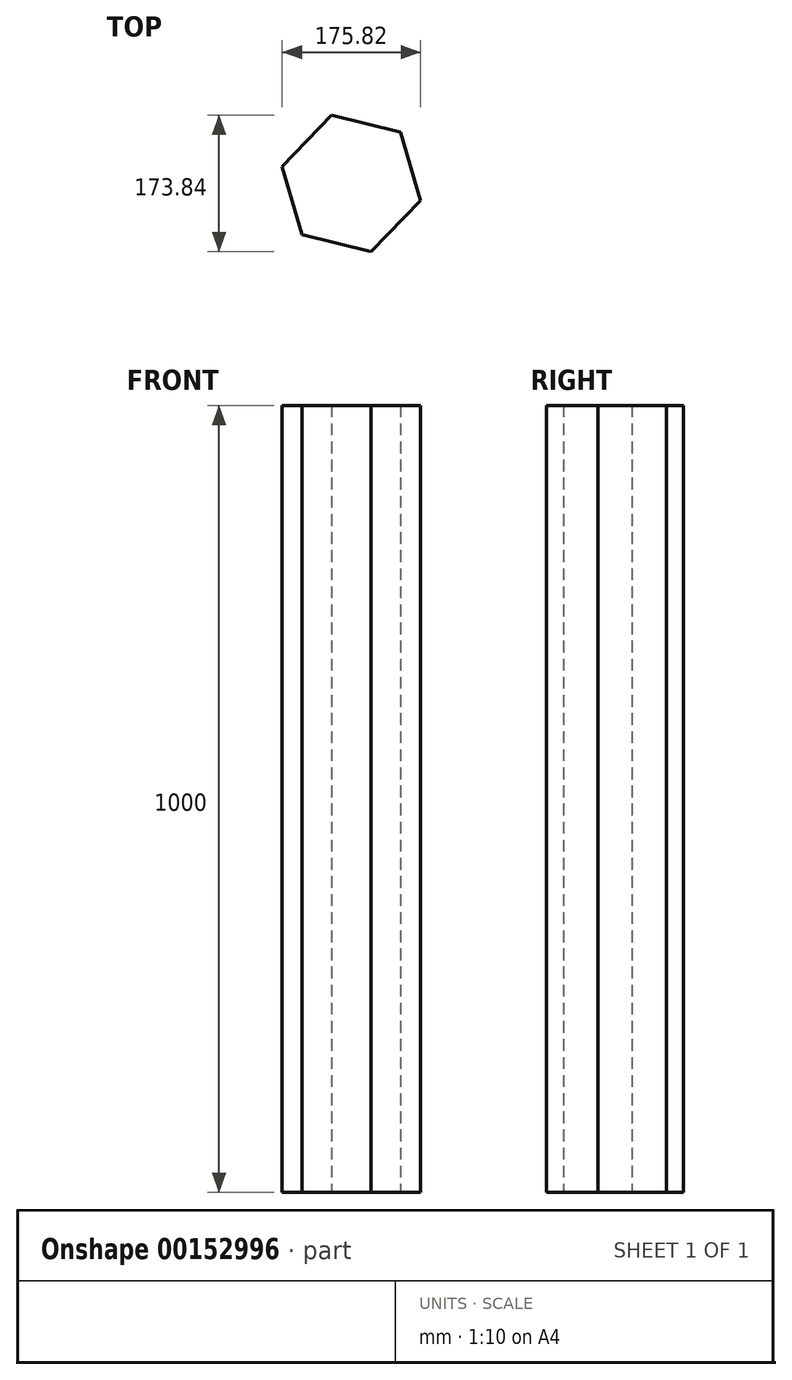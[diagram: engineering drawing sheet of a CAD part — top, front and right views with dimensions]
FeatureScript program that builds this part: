
annotation { "Feature Type Name" : "Feature", "Feature Type Description" : "" }
export const myFeature = defineFeature(function(context is Context, id is Id, definition is map)
    precondition{}
    {
        {
            var Q0;
            Q0=qCreatedBy(makeId("Top.planeOp"),FACE);
            var sketch = newSketch(context, id + "F0", { "sketchPlane" : qUnion([Q0])});
            skCircle(sketch, "E0.cCircle", {"center": v(0, 0) * mm, "radius": 90.52 * mm, "construction": true});
            skLineSegment(sketch, "E0.0", {"start": v(-25.27, 86.92) * mm, "end": v(62.64, 65.35) * mm});
            skLineSegment(sketch, "E0.1", {"start": v(62.64, 65.35) * mm, "end": v(87.91, -21.58) * mm});
            skLineSegment(sketch, "E0.2", {"start": v(87.91, -21.58) * mm, "end": v(25.27, -86.92) * mm});
            skLineSegment(sketch, "E0.3", {"start": v(25.27, -86.92) * mm, "end": v(-62.64, -65.35) * mm});
            skLineSegment(sketch, "E0.4", {"start": v(-62.64, -65.35) * mm, "end": v(-87.91, 21.58) * mm});
            skLineSegment(sketch, "E0.5", {"start": v(-87.91, 21.58) * mm, "end": v(-25.27, 86.92) * mm});
            skSolve(sketch);
        }
        {
            var Q0;
            Q0=makeQuery(id+"F0.imprint","IMPRINT",FACE,{"disambiguationData":[TD([[makeQuery(id+"F0.imprint","IMPRINT",EDGE,{"derivedFrom":sQuery(id+"F0.wireOp",EDGE,"E0.0")}),-1.0]])]});
            extrude(context, id + "F1", {"entities" : qUnion([Q0]), "depth" : 1000 * mm});
        }
    });
